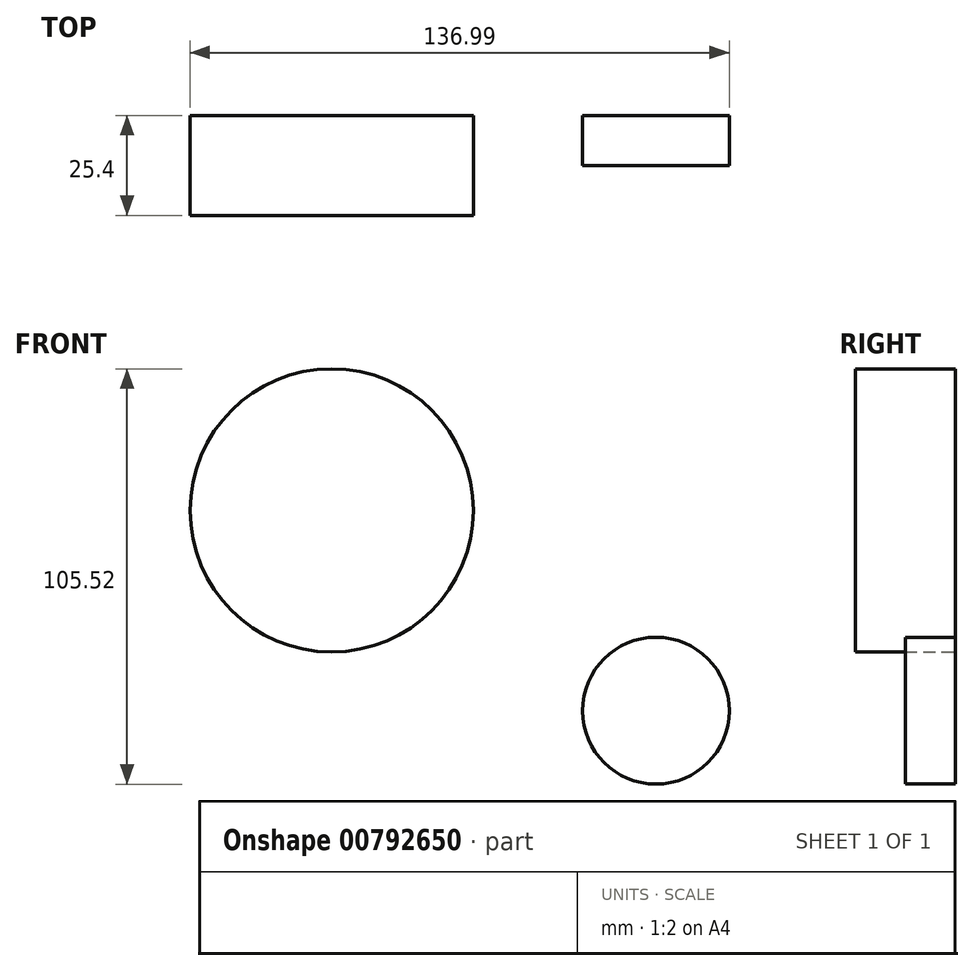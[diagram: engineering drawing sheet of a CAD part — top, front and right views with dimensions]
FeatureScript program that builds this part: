
annotation { "Feature Type Name" : "Feature", "Feature Type Description" : "" }
export const myFeature = defineFeature(function(context is Context, id is Id, definition is map)
    precondition{}
    {
        {
            var Q0;
            Q0=qCreatedBy(makeId("Front.planeOp"),FACE);
            var sketch = newSketch(context, id + "F0", { "sketchPlane" : qUnion([Q0])});
            skCircle(sketch, "E0", {"center": v(0, 0) * mm, "radius": 35.97 * mm});
            skCircle(sketch, "E1", {"center": v(82.37, -50.9) * mm, "radius": 18.65 * mm});
            skLineSegment(sketch, "E2", {"start": v(0, 0) * mm, "end": v(113.23, 0) * mm});
            skCircle(sketch, "E3.MirrorC", {"center": v(82.37, 50.9) * mm, "radius": 18.65 * mm});
            skLineSegment(sketch, "E4", {"start": v(-13.13, 33.49) * mm, "end": v(75.24, 68.13) * mm});
            skLineSegment(sketch, "E5", {"start": v(101.02, 54.31) * mm, "end": v(101.02, -51.13) * mm});
            skLineSegment(sketch, "E6", {"start": v(-13.13, -33.49) * mm, "end": v(81.32, -70.52) * mm});
            skSolve(sketch);
        }
        {
            var Q0;
            {var subQ0=sQuery(id+"F0.wireOp",EDGE,"E0");var subQ1=makeQuery(id+"F0.imprint","IMPRINT",VERTEX,{"derivedFrom":subQ0});Q0=makeQuery(id+"F0.imprint","IMPRINT",FACE,{"disambiguationData":[TD([[makeQuery(id+"F0.imprint","IMPRINT",EDGE,{"disambiguationData":[TD([[subQ1,-1.0]])],"derivedFrom":subQ0}),1.0]])]});}
            extrude(context, id + "F1", {"entities" : qUnion([Q0]), "depth" : 25.4 * mm, "offsetDistance" : 25.4 * mm});
        }
        {
            var Q0;
            {var subQ0=sQuery(id+"F0.wireOp",EDGE,"E1");var subQ1=makeQuery(id+"F0.imprint","INTERSECT",VERTEX,{"derivedFrom":[subQ0,sQuery(id+"F0.wireOp",EDGE,"E5")]});Q0=makeQuery(id+"F0.imprint","IMPRINT",FACE,{"disambiguationData":[TD([[makeQuery(id+"F0.imprint","IMPRINT",EDGE,{"disambiguationData":[TD([[subQ1,-1.0]])],"derivedFrom":subQ0}),1.0]])]});}
            extrude(context, id + "F2", {"entities" : qUnion([Q0]), "operationType" : NewBodyOperationType.ADD, "depth" : 12.7 * mm, "offsetDistance" : 25.4 * mm});
        }
    });
